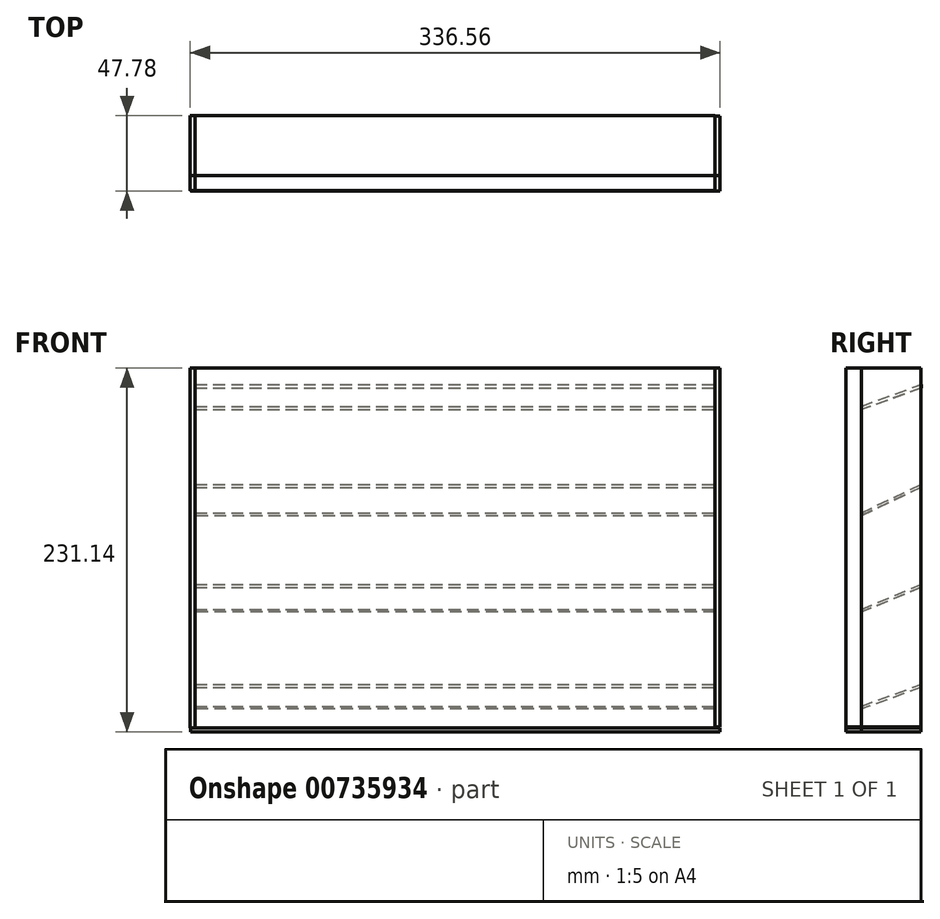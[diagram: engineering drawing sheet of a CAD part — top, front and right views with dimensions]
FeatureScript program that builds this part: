
annotation { "Feature Type Name" : "Feature", "Feature Type Description" : "" }
export const myFeature = defineFeature(function(context is Context, id is Id, definition is map)
    precondition{}
    {
        {
            var Q0;
            Q0=qCreatedBy(makeId("Right.planeOp"),FACE);
            var sketch = newSketch(context, id + "F0", { "sketchPlane" : qUnion([Q0])});
            skLineSegment(sketch, "E0.bottom", {"start": v(-25.44, 174.04) * mm, "end": v(-15.86, 174.04) * mm});
            skLineSegment(sketch, "E0.top", {"start": v(-25.44, -54.56) * mm, "end": v(-15.86, -54.56) * mm});
            skLineSegment(sketch, "E0.left", {"start": v(-25.44, 174.04) * mm, "end": v(-25.44, -54.56) * mm});
            skLineSegment(sketch, "E0.right", {"start": v(-15.86, 174.04) * mm, "end": v(-15.86, -54.56) * mm});
            skSolve(sketch);
        }
        {
            var Q0;
            {var subQ1=sQuery(id+"F0.wireOp",EDGE,"E0.bottom");Q0=makeQuery(id+"F0.imprint","IMPRINT",FACE,{"disambiguationData":[TD([[makeQuery(id+"F0.imprint","IMPRINT",EDGE,{"derivedFrom":subQ1}),-1.0]])]});}
            var Q1;
            {var subQ0=sQuery(id+"F0.wireOp",EDGE,"zDHcUQPE-KDWF-SsUB-WIah-7PEWIp9lFUf2");Q1=makeQuery(id+"F0.imprint","IMPRINT",FACE,{"disambiguationData":[TD([[makeQuery(id+"F0.imprint","IMPRINT",EDGE,{"derivedFrom":subQ0}),-1.0]])]});}
            var Q2;
            {var subQ0=sQuery(id+"F0.wireOp",EDGE,"gfGGJwyZ-6vfu-L9zw-AhdV-NgkuO5Ygg3Zz");Q2=makeQuery(id+"F0.imprint","IMPRINT",FACE,{"disambiguationData":[TD([[makeQuery(id+"F0.imprint","IMPRINT",EDGE,{"derivedFrom":subQ0}),-1.0]])]});}
            var Q3;
            {var subQ0=sQuery(id+"F0.wireOp",EDGE,"tsF7r917-WmZ3-Imur-rxNS-xjG2dlftc75k");Q3=makeQuery(id+"F0.imprint","IMPRINT",FACE,{"disambiguationData":[TD([[makeQuery(id+"F0.imprint","IMPRINT",EDGE,{"derivedFrom":subQ0}),-1.0]])]});}
            extrude(context, id + "F1", {"entities" : qUnion([Q0, Q1, Q2, Q3]), "oppositeDirection" : true, "depth" : 330.2 * mm, "offsetDistance" : 25.4 * mm});
        }
        {
            var Q0;
            Q0=qCreatedBy(makeId("Right.planeOp"),FACE);
            var sketch = newSketch(context, id + "F2", { "sketchPlane" : qUnion([Q0])});
            skLineSegment(sketch, "E1", {"start": v(-16.06, -40.85) * mm, "end": v(22.04, -26.97) * mm});
            skLineSegment(sketch, "E2", {"start": v(-15.91, 20.77) * mm, "end": v(22.19, 36.53) * mm});
            skLineSegment(sketch, "E3", {"start": v(-15.93, 81.99) * mm, "end": v(22.17, 100.03) * mm});
            skLineSegment(sketch, "E4", {"start": v(-15.83, 149.72) * mm, "end": v(22.27, 163.53) * mm});
            skLineSegment(sketch, "E5", {"start": v(-16.06, -40.85) * mm, "end": v(-16.06, -42.71) * mm});
            skLineSegment(sketch, "E6", {"start": v(22.04, -26.97) * mm, "end": v(22.04, -28.9) * mm});
            skLineSegment(sketch, "E7", {"start": v(22.04, -28.9) * mm, "end": v(-16.06, -42.71) * mm});
            skLineSegment(sketch, "E8", {"start": v(-15.91, 20.77) * mm, "end": v(-15.91, 18.93) * mm});
            skLineSegment(sketch, "E9", {"start": v(22.19, 36.53) * mm, "end": v(22.19, 34.64) * mm});
            skLineSegment(sketch, "E10", {"start": v(22.19, 34.64) * mm, "end": v(-15.91, 18.93) * mm});
            skLineSegment(sketch, "E11", {"start": v(-15.93, 81.99) * mm, "end": v(-15.93, 80.13) * mm});
            skLineSegment(sketch, "E12", {"start": v(22.17, 100.03) * mm, "end": v(22.17, 98.2) * mm});
            skLineSegment(sketch, "E13", {"start": v(22.17, 98.2) * mm, "end": v(-15.93, 80.13) * mm});
            skLineSegment(sketch, "E14", {"start": v(-15.83, 149.72) * mm, "end": v(-15.83, 147.52) * mm});
            skLineSegment(sketch, "E15", {"start": v(22.27, 163.53) * mm, "end": v(22.27, 161.32) * mm});
            skLineSegment(sketch, "E16", {"start": v(22.27, 161.32) * mm, "end": v(-15.83, 147.52) * mm});
            skSolve(sketch);
        }
        {
            var Q0;
            Q0 = qSketchRegion(id + "F2", true);
            extrude(context, id + "F3", {"entities" : qUnion([Q0]), "operationType" : NewBodyOperationType.ADD, "oppositeDirection" : true, "depth" : 330.2 * mm, "offsetDistance" : 25.4 * mm});
        }
        {
            var Q0;
            Q0=makeQuery(id+"F3.boolean.opBoolean","MERGE",FACE,{"derivedFrom":[makeQuery(id+"F1.opExtrude","CAP_FACE",FACE,{"disambiguationData":[OSD([sQuery(id+"F0.wireOp",EDGE,"E0.bottom"),sQuery(id+"F0.wireOp",EDGE,"E0.top"),sQuery(id+"F0.wireOp",EDGE,"E0.left"),sQuery(id+"F0.wireOp",EDGE,"E0.right")])],"isStart":false}),makeQuery(id+"F3.opExtrude","CAP_FACE",FACE,{"disambiguationData":[OSD([sQuery(id+"F2.wireOp",EDGE,"E1"),sQuery(id+"F2.wireOp",EDGE,"E5"),sQuery(id+"F2.wireOp",EDGE,"E6"),sQuery(id+"F2.wireOp",EDGE,"E7")])],"isStart":false}),makeQuery(id+"F3.opExtrude","CAP_FACE",FACE,{"disambiguationData":[OSD([sQuery(id+"F2.wireOp",EDGE,"E2"),sQuery(id+"F2.wireOp",EDGE,"E8"),sQuery(id+"F2.wireOp",EDGE,"E9"),sQuery(id+"F2.wireOp",EDGE,"E10")])],"isStart":false}),makeQuery(id+"F3.opExtrude","CAP_FACE",FACE,{"disambiguationData":[OSD([sQuery(id+"F2.wireOp",EDGE,"E3"),sQuery(id+"F2.wireOp",EDGE,"E11"),sQuery(id+"F2.wireOp",EDGE,"E12"),sQuery(id+"F2.wireOp",EDGE,"E13")])],"isStart":false})]});
            var sketch = newSketch(context, id + "F4", { "sketchPlane" : qUnion([Q0])});
            skLineSegment(sketch, "E17.bottom", {"start": v(15.86, 174.04) * mm, "end": v(-22.19, 174.04) * mm});
            skLineSegment(sketch, "E17.top", {"start": v(15.86, -54.47) * mm, "end": v(-22.19, -54.47) * mm});
            skLineSegment(sketch, "E17.left", {"start": v(15.86, 174.04) * mm, "end": v(15.86, -54.47) * mm});
            skLineSegment(sketch, "E17.right", {"start": v(-22.19, 174.04) * mm, "end": v(-22.19, -54.47) * mm});
            skSolve(sketch);
        }
        {
            var Q0;
            Q0 = qSketchRegion(id + "F4", true);
            extrude(context, id + "F5", {"entities" : qUnion([Q0]), "depth" : 3.17 * mm, "offsetDistance" : 25.4 * mm});
        }
        {
            var Q0;
            Q0=makeQuery(id+"F3.boolean.opBoolean","MERGE",FACE,{"derivedFrom":[makeQuery(id+"F1.opExtrude","CAP_FACE",FACE,{"disambiguationData":[OSD([sQuery(id+"F0.wireOp",EDGE,"E0.bottom"),sQuery(id+"F0.wireOp",EDGE,"E0.top"),sQuery(id+"F0.wireOp",EDGE,"E0.left"),sQuery(id+"F0.wireOp",EDGE,"E0.right")])],"isStart":true}),makeQuery(id+"F3.opExtrude","CAP_FACE",FACE,{"disambiguationData":[OSD([sQuery(id+"F2.wireOp",EDGE,"E1"),sQuery(id+"F2.wireOp",EDGE,"E5"),sQuery(id+"F2.wireOp",EDGE,"E6"),sQuery(id+"F2.wireOp",EDGE,"E7")])],"isStart":true}),makeQuery(id+"F3.opExtrude","CAP_FACE",FACE,{"disambiguationData":[OSD([sQuery(id+"F2.wireOp",EDGE,"E2"),sQuery(id+"F2.wireOp",EDGE,"E8"),sQuery(id+"F2.wireOp",EDGE,"E9"),sQuery(id+"F2.wireOp",EDGE,"E10")])],"isStart":true}),makeQuery(id+"F3.opExtrude","CAP_FACE",FACE,{"disambiguationData":[OSD([sQuery(id+"F2.wireOp",EDGE,"E3"),sQuery(id+"F2.wireOp",EDGE,"E11"),sQuery(id+"F2.wireOp",EDGE,"E12"),sQuery(id+"F2.wireOp",EDGE,"E13")])],"isStart":true})]});
            var sketch = newSketch(context, id + "F6", { "sketchPlane" : qUnion([Q0])});
            skLineSegment(sketch, "E18.bottom", {"start": v(-15.86, 174.04) * mm, "end": v(22.04, 174.04) * mm});
            skLineSegment(sketch, "E18.top", {"start": v(-15.86, -54.08) * mm, "end": v(22.04, -54.08) * mm});
            skLineSegment(sketch, "E18.left", {"start": v(-15.86, 174.04) * mm, "end": v(-15.86, -54.08) * mm});
            skLineSegment(sketch, "E18.right", {"start": v(22.04, 174.04) * mm, "end": v(22.04, -54.08) * mm});
            skSolve(sketch);
        }
        {
            var Q0;
            Q0 = qSketchRegion(id + "F6", true);
            extrude(context, id + "F7", {"entities" : qUnion([Q0]), "depth" : 3.17 * mm, "offsetDistance" : 25.4 * mm});
        }
        {
            var Q0;
            Q0=makeQuery(id+"F1.opExtrude","SWEPT_FACE",FACE,{"disambiguationData":[OSD([sQuery(id+"F0.wireOp",EDGE,"E0.top")])]});
            var sketch = newSketch(context, id + "F8", { "sketchPlane" : qUnion([Q0])});
            skLineSegment(sketch, "E19.bottom", {"start": v(-333, 15.86) * mm, "end": v(3.18, 15.86) * mm});
            skLineSegment(sketch, "E19.top", {"start": v(-333, -22.04) * mm, "end": v(3.18, -22.04) * mm});
            skLineSegment(sketch, "E19.left", {"start": v(-333, 15.86) * mm, "end": v(-333, -22.04) * mm});
            skLineSegment(sketch, "E19.right", {"start": v(3.18, 15.86) * mm, "end": v(3.18, -22.04) * mm});
            skSolve(sketch);
        }
        {
            var Q0;
            Q0 = qSketchRegion(id + "F8", true);
            extrude(context, id + "F9", {"entities" : qUnion([Q0]), "depth" : 2.54 * mm, "offsetDistance" : 25.4 * mm});
        }
        {
            var Q0;
            Q0=makeQuery(id+"F5.opExtrude","SWEPT_FACE",FACE,{"disambiguationData":[OSD([sQuery(id+"F4.wireOp",EDGE,"E17.left")])]});
            extrude(context, id + "F10", {"entities" : qUnion([Q0]), "depth" : 9.4 * mm, "offsetDistance" : 25.4 * mm});
        }
        {
            var Q0;
            Q0=makeQuery(id+"F9.opExtrude","SWEPT_FACE",FACE,{"disambiguationData":[OSD([sQuery(id+"F8.wireOp",EDGE,"E19.bottom")])]});
            extrude(context, id + "F11", {"entities" : qUnion([Q0]), "depth" : 9.65 * mm, "offsetDistance" : 25.4 * mm});
        }
        {
            var Q0;
            Q0=makeQuery(id+"F7.opExtrude","SWEPT_FACE",FACE,{"disambiguationData":[OSD([sQuery(id+"F6.wireOp",EDGE,"E18.left")])]});
            extrude(context, id + "F12", {"entities" : qUnion([Q0]), "depth" : 9.65 * mm, "offsetDistance" : 25.4 * mm});
        }
    });
